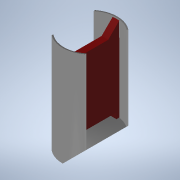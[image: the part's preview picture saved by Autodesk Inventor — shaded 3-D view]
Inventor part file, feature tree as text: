
AUTODESK INVENTOR PART (.ipt)
format: ipt  version: 2021.3 (Build 253353010, 353A)  size: 142,848 bytes
history: native  units: mm
features: extrude x5, sketch x5, plane x2, chamfer x1
ambient origin geometry x8: Origin, YZ Plane, XZ Plane, XY Plane, X Axis, Y Axis, Z Axis, Center Point
bodies: Solid1 (feature_tree), Solid2 (feature_tree)
feature tree (13):
  extrude  "Extrusion1"  Depth=121.0mm TaperAngle=0.0deg
  extrude  "Extrusion2"  Depth=103.0mm TaperAngle=0.0deg
  extrude  "Extrusion4"  Depth=15.0mm
  plane  "Work Plane1"
  plane  "Work Plane2"
  extrude  "Extrusion5"  Depth=8.0mm TaperAngle=0.0deg
  extrude  "Extrusion6"  Depth=3.5mm TaperAngle=0.0deg
  chamfer  "Chamfer5"  Distance=100.0mm
  sketch  "Sketch1"  dims[d0=66.0mm d1=121.0mm d2=0.0mm]
  sketch  "Sketch2"  dims[d3=63.0mm d4=103.0mm d5=0.0mm]
  sketch  "Sketch3"  dims[d13=25.0mm d17=15.0mm]
  sketch  "Sketch4"  dims[d19=15.0mm d20=8.0mm d21=0.0mm]
  sketch  "Sketch5"  dims[d22=20.0mm d23=-20.0mm d24=100.0mm d25=0.0mm d26=100.0mm d27=0.0mm d33=3.5mm d46=20.0mm d47=2.0mm d48=45.0deg]
